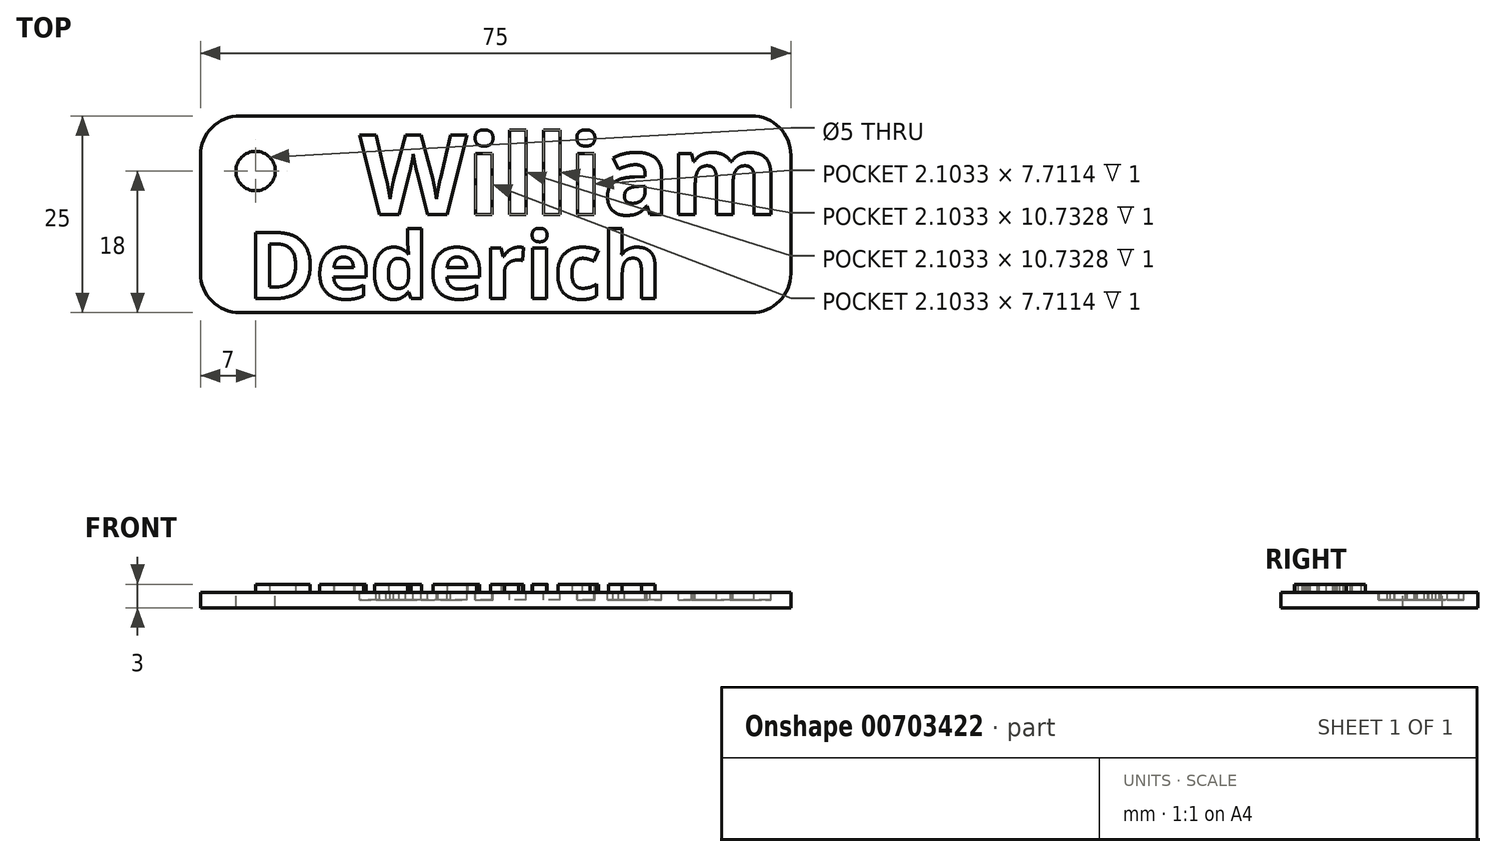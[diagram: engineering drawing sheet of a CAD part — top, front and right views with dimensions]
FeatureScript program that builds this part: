
annotation { "Feature Type Name" : "Feature", "Feature Type Description" : "" }
export const myFeature = defineFeature(function(context is Context, id is Id, definition is map)
    precondition{}
    {
        {
            var Q0;
            Q0=qCreatedBy(makeId("Top.planeOp"),FACE);
            var sketch = newSketch(context, id + "F0", { "sketchPlane" : qUnion([Q0])});
            skLineSegment(sketch, "E0.bottom", {"start": v(-32.5, 12.5) * mm, "end": v(32.5, 12.5) * mm});
            skLineSegment(sketch, "E0.top", {"start": v(-32.5, -12.5) * mm, "end": v(32.5, -12.5) * mm});
            skLineSegment(sketch, "E0.left", {"start": v(-37.5, 7.5) * mm, "end": v(-37.5, -7.5) * mm});
            skLineSegment(sketch, "E0.right", {"start": v(37.5, 7.5) * mm, "end": v(37.5, -7.5) * mm});
            skPoint(sketch, "E0.middle", {"position": v(0, 0) * mm});
            skPoint(sketch, "E1.visualSharp", {"position": v(-37.5, 12.5) * mm});
            skArc(sketch, "E1.filletArc", {"start": v(-32.5, 12.5) * mm, "mid": v(-36.04, 11.04) * mm, "end": v(-37.5, 7.5) * mm});
            skPoint(sketch, "E2.visualSharp", {"position": v(-37.5, -12.5) * mm});
            skArc(sketch, "E2.filletArc", {"start": v(-37.5, -7.5) * mm, "mid": v(-36.04, -11.04) * mm, "end": v(-32.5, -12.5) * mm});
            skPoint(sketch, "E3.visualSharp", {"position": v(37.5, -12.5) * mm});
            skArc(sketch, "E3.filletArc", {"start": v(32.5, -12.5) * mm, "mid": v(36.04, -11.04) * mm, "end": v(37.5, -7.5) * mm});
            skPoint(sketch, "E4.visualSharp", {"position": v(37.5, 12.5) * mm});
            skArc(sketch, "E4.filletArc", {"start": v(37.5, 7.5) * mm, "mid": v(36.04, 11.04) * mm, "end": v(32.5, 12.5) * mm});
            skSolve(sketch);
        }
        {
            var Q0;
            Q0 = qSketchRegion(id + "F0", true);
            extrude(context, id + "F1", {"entities" : qUnion([Q0]), "depth" : 2 * mm, "offsetDistance" : 25 * mm});
        }
        {
            var Q0;
            Q0=makeQuery(id+"F1.opExtrude","CAP_FACE",FACE,{"disambiguationData":[OSD([sQuery(id+"F0.wireOp",EDGE,"E0.bottom"),sQuery(id+"F0.wireOp",EDGE,"E0.top"),sQuery(id+"F0.wireOp",EDGE,"E0.left"),sQuery(id+"F0.wireOp",EDGE,"E0.right"),sQuery(id+"F0.wireOp",EDGE,"E1.filletArc"),sQuery(id+"F0.wireOp",EDGE,"E2.filletArc"),sQuery(id+"F0.wireOp",EDGE,"E3.filletArc"),sQuery(id+"F0.wireOp",EDGE,"E4.filletArc")])],"isStart":false});
            var sketch = newSketch(context, id + "F2", { "sketchPlane" : qUnion([Q0])});
            skPoint(sketch, "E5", {"position": v(-30.5, 5.5) * mm});
            skPoint(sketch, "E6", {"position": v(-37.5, 7.5) * mm});
            skPoint(sketch, "E7", {"position": v(-32.5, 12.5) * mm});
            skSolve(sketch);
        }
        {
            var Q0;
            Q0=sQuery(id+"F2.wireOp",VERTEX,"E5");
            var Q1;
            Q1=makeQuery(id+"F1.opExtrude","SWEPT_BODY",BODY,{"disambiguationData":[OSD([sQuery(id+"F0.wireOp",EDGE,"E0.bottom"),sQuery(id+"F0.wireOp",EDGE,"E0.top"),sQuery(id+"F0.wireOp",EDGE,"E0.left"),sQuery(id+"F0.wireOp",EDGE,"E0.right"),sQuery(id+"F0.wireOp",EDGE,"E1.filletArc"),sQuery(id+"F0.wireOp",EDGE,"E2.filletArc"),sQuery(id+"F0.wireOp",EDGE,"E3.filletArc"),sQuery(id+"F0.wireOp",EDGE,"E4.filletArc")])]});
            hole(context, id + "F3", {"style" : HoleStyle.SIMPLE, "endStyle" : HoleEndStyle.THROUGH, "holeDiameter" : 5 * mm, "majorDiameter" : 5 * mm, "isTappedThrough" : true, "tappedDepth" : 12 * mm, "tapClearance" : 3, "locations" : qUnion([Q0]), "scope" : qUnion([Q1])});
        }
        {
            var Q0;
            Q0=makeQuery(id+"F1.opExtrude","CAP_FACE",FACE,{"disambiguationData":[OSD([sQuery(id+"F0.wireOp",EDGE,"E0.bottom"),sQuery(id+"F0.wireOp",EDGE,"E0.top"),sQuery(id+"F0.wireOp",EDGE,"E0.left"),sQuery(id+"F0.wireOp",EDGE,"E0.right"),sQuery(id+"F0.wireOp",EDGE,"E1.filletArc"),sQuery(id+"F0.wireOp",EDGE,"E2.filletArc"),sQuery(id+"F0.wireOp",EDGE,"E3.filletArc"),sQuery(id+"F0.wireOp",EDGE,"E4.filletArc")])],"isStart":false});
            var sketch = newSketch(context, id + "F4", { "sketchPlane" : qUnion([Q0])});
            skText(sketch, "E8", { "text": "William", "fontName": "OpenSans-Bold.ttf"});
            const initialGuessF4  = {"E8": [-0.0173, 0, 1, 0, 0.01017]};
            skSetInitialGuess(sketch, initialGuessF4);
            skSolve(sketch);
        }
        {
            var Q0;
            Q0 = qSketchRegion(id + "F4", true);
            extrude(context, id + "F5", {"entities" : qUnion([Q0]), "operationType" : NewBodyOperationType.REMOVE, "oppositeDirection" : true, "depth" : 1 * mm, "offsetDistance" : 25 * mm});
        }
        {
            var Q0;
            Q0=makeQuery(id+"F4.imprint","IMPRINT",FACE,{"disambiguationData":[TD([[makeQuery(id+"F4.imprint","IMPRINT",EDGE,{"derivedFrom":sQuery(id+"F4.wireOp",EDGE,"E8.sketch_text.stroke-0")}),1.0]])]});
            var sketch = newSketch(context, id + "F6", { "sketchPlane" : qUnion([Q0])});
            skText(sketch, "E9", { "text": "Dederich", "fontName": "OpenSans-Bold.ttf"});
            const initialGuessF6  = {"E9": [-0.03158, -0.0107, 1, 0, 0.00846]};
            skSetInitialGuess(sketch, initialGuessF6);
            skSolve(sketch);
        }
        {
            var Q0;
            Q0 = qSketchRegion(id + "F6", true);
            extrude(context, id + "F7", {"entities" : qUnion([Q0]), "operationType" : NewBodyOperationType.ADD, "depth" : 1 * mm, "offsetDistance" : 25 * mm});
        }
    });
